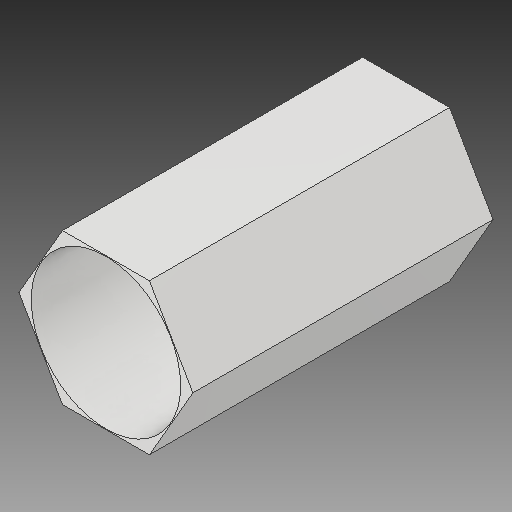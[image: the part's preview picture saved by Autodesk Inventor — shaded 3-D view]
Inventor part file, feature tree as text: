
AUTODESK INVENTOR PART (.ipt)
format: ipt  version: 2017 (Build 210142000, 142)  size: 98,304 bytes
history: native  units: in
note: dims shown in document units (in); Inventor stores cm internally (conversion verified against a paired STEP export)
features: extrude x1, sketch x1
ambient origin geometry x8: Origin, YZ Plane, XZ Plane, XY Plane, X Axis, Y Axis, Z Axis, Center Point
bodies: Solid1 (feature_tree)
feature tree (2):
  extrude  "Extrusion1"  Depth=1.0in TaperAngle=0.0deg
  sketch  "Sketch1"  dims[d0=0.498in d1=1.0in d2=0.0in]
